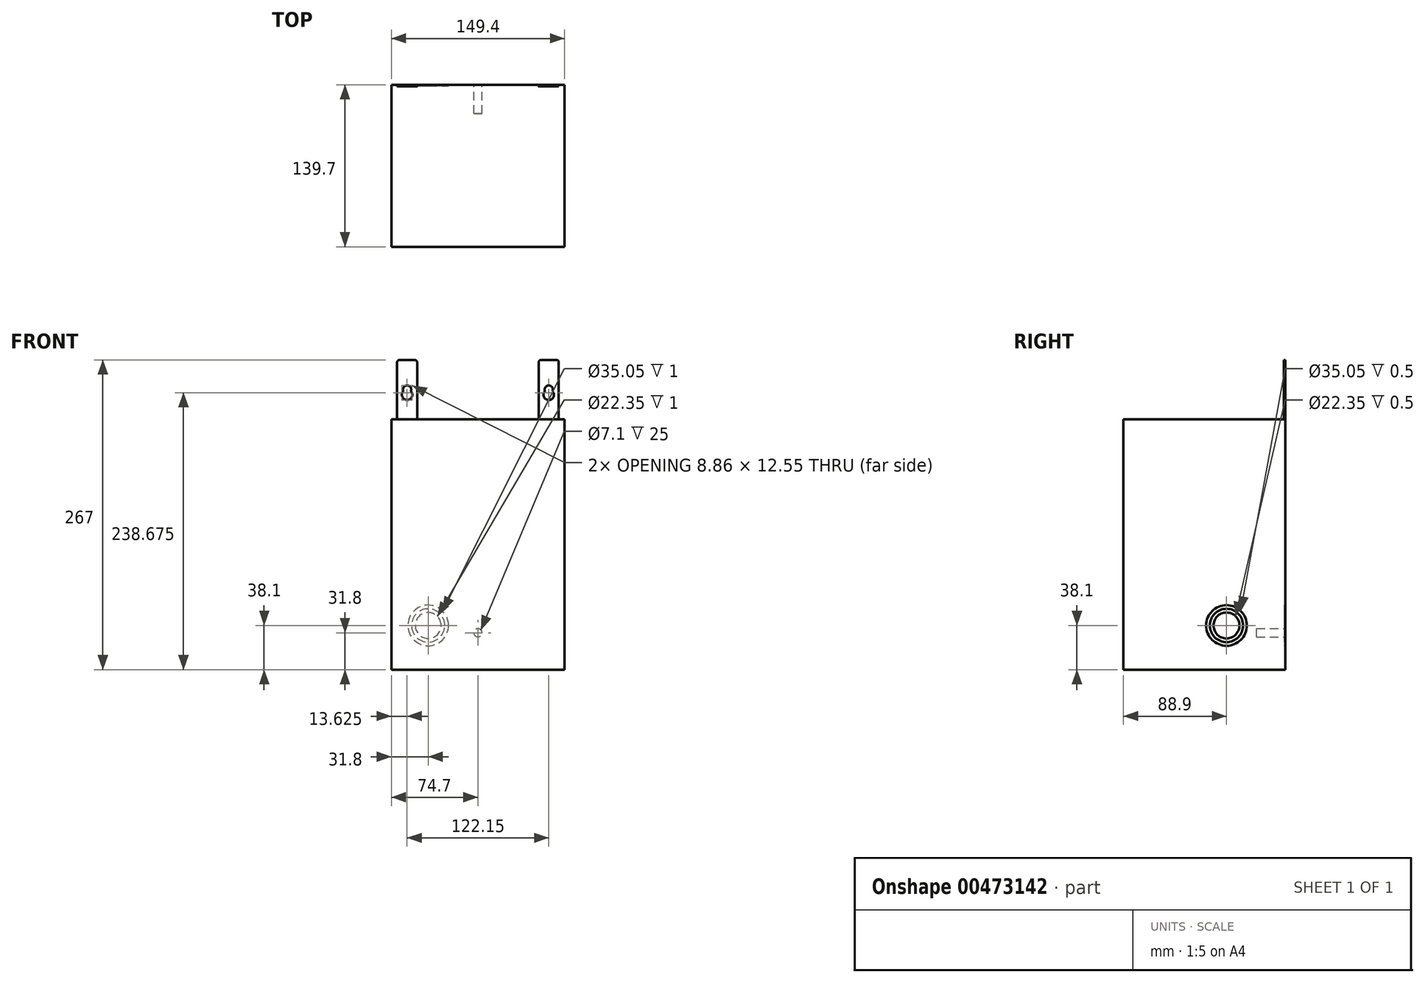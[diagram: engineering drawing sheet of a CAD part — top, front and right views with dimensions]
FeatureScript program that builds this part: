
annotation { "Feature Type Name" : "Feature", "Feature Type Description" : "" }
export const myFeature = defineFeature(function(context is Context, id is Id, definition is map)
    precondition{}
    {
        {
            var Q0;
            Q0=qCreatedBy(makeId("Right.planeOp"),FACE);
            var sketch = newSketch(context, id + "F0", { "sketchPlane" : qUnion([Q0])});
            skLineSegment(sketch, "E0", {"start": v(0, 0) * mm, "end": v(0, 215.9) * mm});
            skLineSegment(sketch, "E1", {"start": v(0, 215.9) * mm, "end": v(139.7, 215.9) * mm});
            skLineSegment(sketch, "E2", {"start": v(0, 0) * mm, "end": v(139.7, 0) * mm});
            skLineSegment(sketch, "E3", {"start": v(139.7, 0) * mm, "end": v(139.7, 215.9) * mm});
            skSolve(sketch);
        }
        {
            var Q0;
            Q0=makeQuery(id+"F0.imprint","IMPRINT",FACE,{"disambiguationData":[TD([[makeQuery(id+"F0.imprint","IMPRINT",EDGE,{"derivedFrom":sQuery(id+"F0.wireOp",EDGE,"E0")}),-1.0]])]});
            extrude(context, id + "F1", {"entities" : qUnion([Q0]), "endBound" : BoundingType.SYMMETRIC, "depth" : 149.4 * mm});
        }
        {
            var Q0;
            Q0=makeQuery(id+"F1.opExtrude","CAP_FACE",FACE,{"disambiguationData":[OSD([sQuery(id+"F0.wireOp",EDGE,"E0"),sQuery(id+"F0.wireOp",EDGE,"E1"),sQuery(id+"F0.wireOp",EDGE,"E2"),sQuery(id+"F0.wireOp",EDGE,"E3")])],"isStart":false});
            var sketch = newSketch(context, id + "F2", { "sketchPlane" : qUnion([Q0])});
            skCircle(sketch, "E4", {"center": v(88.9, 38.1) * mm, "radius": 11.18 * mm});
            skCircle(sketch, "E5", {"center": v(88.9, 38.1) * mm, "radius": 14.35 * mm});
            skCircle(sketch, "E6", {"center": v(88.9, 38.1) * mm, "radius": 17.53 * mm});
            skSolve(sketch);
        }
        {
            var Q0;
            Q0=makeQuery(id+"F2.imprint","IMPRINT",FACE,{"disambiguationData":[TD([[makeQuery(id+"F2.imprint","IMPRINT",EDGE,{"derivedFrom":sQuery(id+"F2.wireOp",EDGE,"E5")}),-1.0]])]});
            var Q1;
            Q1=makeQuery(id+"F2.imprint","IMPRINT",FACE,{"disambiguationData":[TD([[makeQuery(id+"F2.imprint","IMPRINT",EDGE,{"derivedFrom":sQuery(id+"F2.wireOp",EDGE,"E4")}),1.0]])]});
            extrude(context, id + "F3", {"entities" : qUnion([Q0, Q1]), "operationType" : NewBodyOperationType.REMOVE, "oppositeDirection" : true, "depth" : 0.5 * mm});
        }
        {
            var Q0;
            Q0=makeQuery(id+"F1.opExtrude","SWEPT_FACE",FACE,{"disambiguationData":[OSD([sQuery(id+"F0.wireOp",EDGE,"E3")])]});
            var sketch = newSketch(context, id + "F4", { "sketchPlane" : qUnion([Q0])});
            skCircle(sketch, "E7", {"center": v(42.9, 38.1) * mm, "radius": 11.18 * mm});
            skCircle(sketch, "E8", {"center": v(42.9, 38.1) * mm, "radius": 14.35 * mm});
            skCircle(sketch, "E9", {"center": v(42.9, 38.1) * mm, "radius": 17.53 * mm});
            skCircle(sketch, "E10", {"center": v(0, 31.8) * mm, "radius": 3.55 * mm});
            skCircle(sketch, "E11", {"center": v(0, 31.8) * mm, "radius": 5 * mm});
            skLineSegment(sketch, "E12", {"start": v(-74.7, 210.9) * mm, "end": v(74.7, 210.9) * mm});
            skSolve(sketch);
        }
        {
            var Q0;
            Q0=makeQuery(id+"F4.imprint","IMPRINT",FACE,{"disambiguationData":[TD([[makeQuery(id+"F4.imprint","IMPRINT",EDGE,{"derivedFrom":sQuery(id+"F4.wireOp",EDGE,"E8")}),-1.0]])]});
            var Q1;
            Q1=makeQuery(id+"F4.imprint","IMPRINT",FACE,{"disambiguationData":[TD([[makeQuery(id+"F4.imprint","IMPRINT",EDGE,{"derivedFrom":sQuery(id+"F4.wireOp",EDGE,"E7")}),1.0]])]});
            extrude(context, id + "F5", {"entities" : qUnion([Q0, Q1]), "operationType" : NewBodyOperationType.REMOVE, "oppositeDirection" : true, "depth" : 1 * mm});
        }
        {
            var Q0;
            Q0=makeQuery(id+"F4.imprint","IMPRINT",FACE,{"disambiguationData":[TD([[makeQuery(id+"F4.imprint","IMPRINT",EDGE,{"derivedFrom":sQuery(id+"F4.wireOp",EDGE,"E10")}),1.0]])]});
            extrude(context, id + "F6", {"entities" : qUnion([Q0]), "operationType" : NewBodyOperationType.REMOVE, "oppositeDirection" : true, "depth" : 25 * mm});
        }
        {
            var Q0;
            Q0=makeQuery(id+"F1.opExtrude","SWEPT_FACE",FACE,{"disambiguationData":[OSD([sQuery(id+"F0.wireOp",EDGE,"E1")])]});
            var sketch = newSketch(context, id + "F7", { "sketchPlane" : qUnion([Q0])});
            skLineSegment(sketch, "E13.bottom", {"start": v(69.7, 139.7) * mm, "end": v(52.45, 139.7) * mm});
            skLineSegment(sketch, "E13.top", {"start": v(69.7, 138.3) * mm, "end": v(52.45, 138.3) * mm});
            skLineSegment(sketch, "E13.left", {"start": v(69.7, 139.7) * mm, "end": v(69.7, 138.3) * mm});
            skLineSegment(sketch, "E13.right", {"start": v(52.45, 139.7) * mm, "end": v(52.45, 138.3) * mm});
            skLineSegment(sketch, "E14.MirrorCS", {"start": v(-69.7, 138.3) * mm, "end": v(-52.45, 138.3) * mm});
            skLineSegment(sketch, "E15.MirrorCS", {"start": v(-69.7, 139.7) * mm, "end": v(-52.45, 139.7) * mm});
            skLineSegment(sketch, "E16.MirrorCS", {"start": v(-69.7, 139.7) * mm, "end": v(-69.7, 138.3) * mm});
            skLineSegment(sketch, "E17.MirrorCS", {"start": v(-52.45, 139.7) * mm, "end": v(-52.45, 138.3) * mm});
            skSolve(sketch);
        }
        {
            var Q0;
            Q0=makeQuery(id+"F7.imprint","IMPRINT",FACE,{"disambiguationData":[TD([[makeQuery(id+"F7.imprint","IMPRINT",EDGE,{"derivedFrom":sQuery(id+"F7.wireOp",EDGE,"E13.bottom")}),1.0]])]});
            var Q1;
            Q1=makeQuery(id+"F7.imprint","IMPRINT",FACE,{"disambiguationData":[TD([[makeQuery(id+"F7.imprint","IMPRINT",EDGE,{"derivedFrom":sQuery(id+"F7.wireOp",EDGE,"E14.MirrorCS")}),1.0]])]});
            extrude(context, id + "F8", {"entities" : qUnion([Q0, Q1]), "operationType" : NewBodyOperationType.ADD, "depth" : 51.1 * mm});
        }
        {
            var Q0;
            {var subQ1=sQuery(id+"F0.wireOp",EDGE,"E1");var subQ2=sQuery(id+"F0.wireOp",EDGE,"E3");Q0=makeQuery(id+"F8.boolean.opBoolean","MERGE",FACE,{"derivedFrom":[makeQuery(id+"F5.boolean.opBoolean","SPLIT",FACE,{"disambiguationData":[TD([makeQuery(id+"F1.opExtrude","SWEPT_FACE",FACE,{"disambiguationData":[OSD([subQ1])]})])],"derivedFrom":makeQuery(id+"F1.opExtrude","SWEPT_FACE",FACE,{"disambiguationData":[OSD([subQ2])]})}),makeQuery(id+"F8.opExtrude","SWEPT_FACE",FACE,{"disambiguationData":[OSD([sQuery(id+"F7.wireOp",EDGE,"E13.bottom")])]}),makeQuery(id+"F8.opExtrude","SWEPT_FACE",FACE,{"disambiguationData":[OSD([sQuery(id+"F7.wireOp",EDGE,"E15.MirrorCS")])]})]});}
            var sketch = newSketch(context, id + "F9", { "sketchPlane" : qUnion([Q0])});
            skCircle(sketch, "E18", {"center": v(-61.08, 241.4) * mm, "radius": 3.55 * mm});
            skPoint(sketch, "E18.centerSnap0", {"position": v(-61.08, 267) * mm});
            skCircle(sketch, "E19", {"center": v(61.08, 241.4) * mm, "radius": 3.55 * mm});
            skPoint(sketch, "E19.centerSnap0", {"position": v(61.08, 267) * mm});
            skCircle(sketch, "E20", {"center": v(-61.08, 236.9) * mm, "radius": 4.5 * mm});
            skCircle(sketch, "E21", {"center": v(61.08, 236.9) * mm, "radius": 4.5 * mm});
            skSolve(sketch);
        }
        {
            var Q0;
            {var subQ0=sQuery(id+"F9.wireOp",EDGE,"E20");var subQ1=sQuery(id+"F9.wireOp",EDGE,"E18");var subQ2=makeQuery(id+"F9.imprint","INTERSECT",VERTEX,{"disambiguationData":[OD(0.0)],"derivedFrom":[subQ1,subQ0]});Q0=makeQuery(id+"F9.imprint","IMPRINT",FACE,{"disambiguationData":[TD([[makeQuery(id+"F9.imprint","IMPRINT",EDGE,{"disambiguationData":[TD([[subQ2,-1.0]])],"derivedFrom":subQ1}),1.0]])]});}
            var Q1;
            {var subQ0=sQuery(id+"F9.wireOp",EDGE,"E20");var subQ1=sQuery(id+"F9.wireOp",EDGE,"E18");var subQ2=makeQuery(id+"F9.imprint","INTERSECT",VERTEX,{"disambiguationData":[OD(0.0)],"derivedFrom":[subQ1,subQ0]});Q1=makeQuery(id+"F9.imprint","IMPRINT",FACE,{"disambiguationData":[TD([[makeQuery(id+"F9.imprint","IMPRINT",EDGE,{"disambiguationData":[TD([[subQ2,1.0]])],"derivedFrom":subQ1}),1.0]])]});}
            var Q2;
            {var subQ0=sQuery(id+"F9.wireOp",EDGE,"E20");var subQ1=sQuery(id+"F9.wireOp",EDGE,"E18");var subQ2=makeQuery(id+"F9.imprint","INTERSECT",VERTEX,{"disambiguationData":[OD(0.0)],"derivedFrom":[subQ1,subQ0]});Q2=makeQuery(id+"F9.imprint","IMPRINT",FACE,{"disambiguationData":[TD([[makeQuery(id+"F9.imprint","IMPRINT",EDGE,{"disambiguationData":[TD([[subQ2,1.0]])],"derivedFrom":subQ1}),-1.0]])]});}
            var Q3;
            {var subQ0=sQuery(id+"F9.wireOp",EDGE,"E21");var subQ1=sQuery(id+"F9.wireOp",EDGE,"E19");var subQ2=makeQuery(id+"F9.imprint","INTERSECT",VERTEX,{"disambiguationData":[OD(0.0)],"derivedFrom":[subQ1,subQ0]});Q3=makeQuery(id+"F9.imprint","IMPRINT",FACE,{"disambiguationData":[TD([[makeQuery(id+"F9.imprint","IMPRINT",EDGE,{"disambiguationData":[TD([[subQ2,-1.0]])],"derivedFrom":subQ1}),1.0]])]});}
            var Q4;
            {var subQ0=sQuery(id+"F9.wireOp",EDGE,"E21");var subQ1=sQuery(id+"F9.wireOp",EDGE,"E19");var subQ2=makeQuery(id+"F9.imprint","INTERSECT",VERTEX,{"disambiguationData":[OD(0.0)],"derivedFrom":[subQ1,subQ0]});Q4=makeQuery(id+"F9.imprint","IMPRINT",FACE,{"disambiguationData":[TD([[makeQuery(id+"F9.imprint","IMPRINT",EDGE,{"disambiguationData":[TD([[subQ2,1.0]])],"derivedFrom":subQ1}),1.0]])]});}
            var Q5;
            {var subQ0=sQuery(id+"F9.wireOp",EDGE,"E21");var subQ1=sQuery(id+"F9.wireOp",EDGE,"E19");var subQ2=makeQuery(id+"F9.imprint","INTERSECT",VERTEX,{"disambiguationData":[OD(0.0)],"derivedFrom":[subQ1,subQ0]});Q5=makeQuery(id+"F9.imprint","IMPRINT",FACE,{"disambiguationData":[TD([[makeQuery(id+"F9.imprint","IMPRINT",EDGE,{"disambiguationData":[TD([[subQ2,1.0]])],"derivedFrom":subQ1}),-1.0]])]});}
            extrude(context, id + "F10", {"entities" : qUnion([Q0, Q1, Q2, Q3, Q4, Q5]), "operationType" : NewBodyOperationType.REMOVE, "endBound" : BoundingType.THROUGH_ALL, "oppositeDirection" : true, "depth" : 25 * mm});
        }
        {
            var Q0;
            Q0=makeQuery(id+"F8.opExtrude","CAP_EDGE",EDGE,{"disambiguationData":[OSD([sQuery(id+"F7.wireOp",EDGE,"E17.MirrorCS")])],"isStart":false});
            var Q1;
            Q1=makeQuery(id+"F8.opExtrude","CAP_EDGE",EDGE,{"disambiguationData":[OSD([sQuery(id+"F7.wireOp",EDGE,"E16.MirrorCS")])],"isStart":false});
            var Q2;
            Q2=makeQuery(id+"F8.opExtrude","CAP_EDGE",EDGE,{"disambiguationData":[OSD([sQuery(id+"F7.wireOp",EDGE,"E13.left")])],"isStart":false});
            var Q3;
            Q3=makeQuery(id+"F8.opExtrude","CAP_EDGE",EDGE,{"disambiguationData":[OSD([sQuery(id+"F7.wireOp",EDGE,"E13.right")])],"isStart":false});
            fillet(context, id + "F11", {"entities" : qUnion([Q0, Q1, Q2, Q3]), "radius" : 2 * mm, "tangentPropagation" : true, "allowEdgeOverflow" : false});
        }
    });
